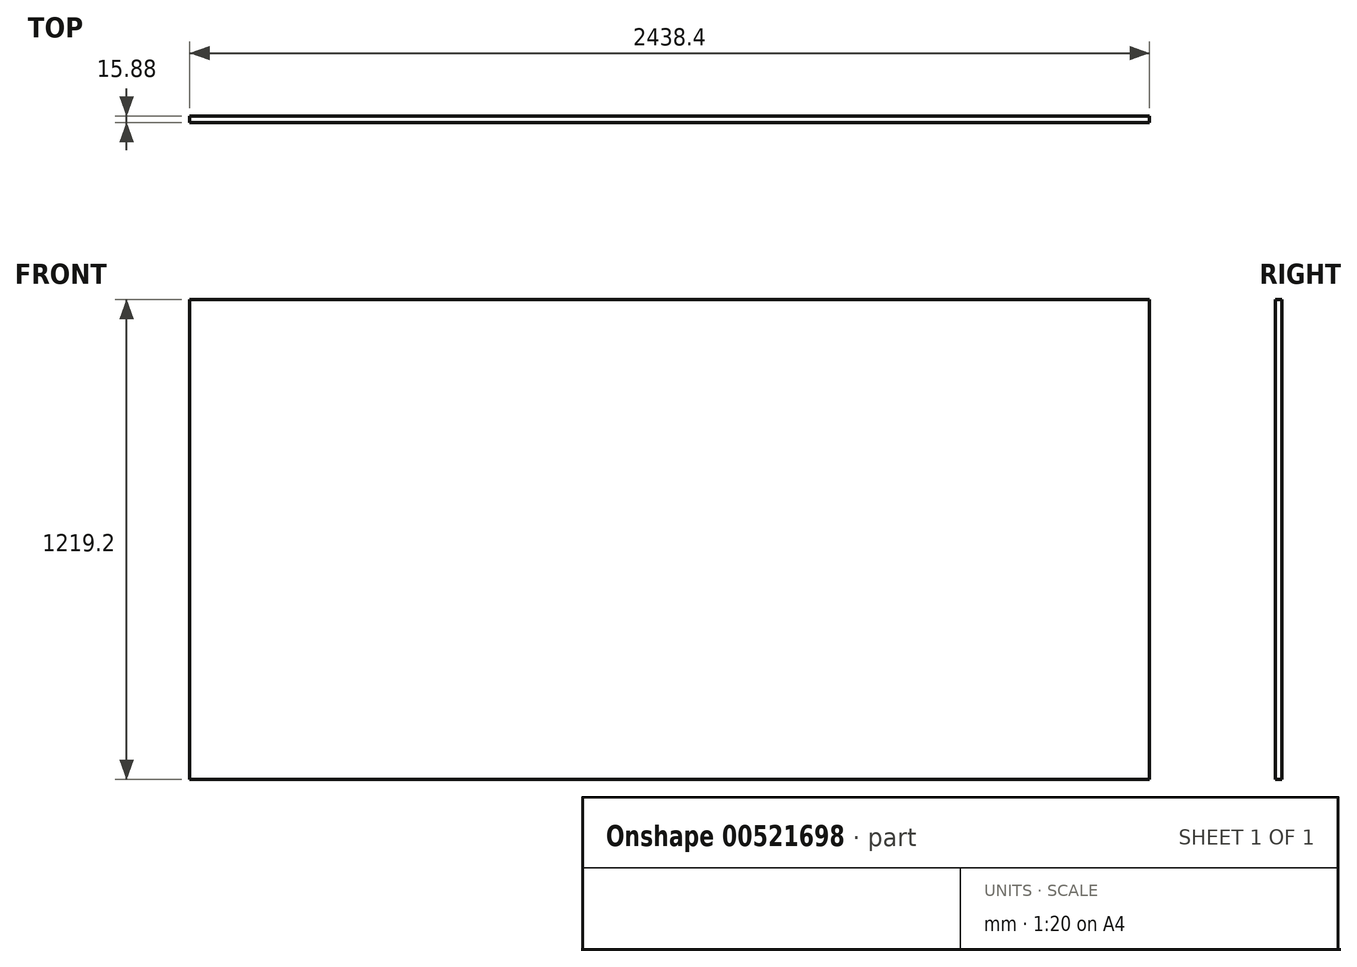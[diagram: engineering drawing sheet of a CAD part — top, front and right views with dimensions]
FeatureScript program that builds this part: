
annotation { "Feature Type Name" : "Feature", "Feature Type Description" : "" }
export const myFeature = defineFeature(function(context is Context, id is Id, definition is map)
    precondition{}
    {
        {
            var Q0;
            Q0=qCreatedBy(makeId("Front.planeOp"),FACE);
            var sketch = newSketch(context, id + "F0", { "sketchPlane" : qUnion([Q0])});
            skLineSegment(sketch, "E0.bottom", {"start": v(1219.2, 609.6) * mm, "end": v(-1219.2, 609.6) * mm});
            skLineSegment(sketch, "E0.top", {"start": v(1219.2, -609.6) * mm, "end": v(-1219.2, -609.6) * mm});
            skLineSegment(sketch, "E0.left", {"start": v(1219.2, 609.6) * mm, "end": v(1219.2, -609.6) * mm});
            skLineSegment(sketch, "E0.right", {"start": v(-1219.2, 609.6) * mm, "end": v(-1219.2, -609.6) * mm});
            skPoint(sketch, "E0.middle", {"position": v(0, 0) * mm});
            skSolve(sketch);
        }
        {
            var Q0;
            Q0 = qSketchRegion(id + "F0", true);
            extrude(context, id + "F1", {"entities" : qUnion([Q0]), "depth" : 15.88 * mm, "offsetDistance" : 25.4 * mm});
        }
    });
